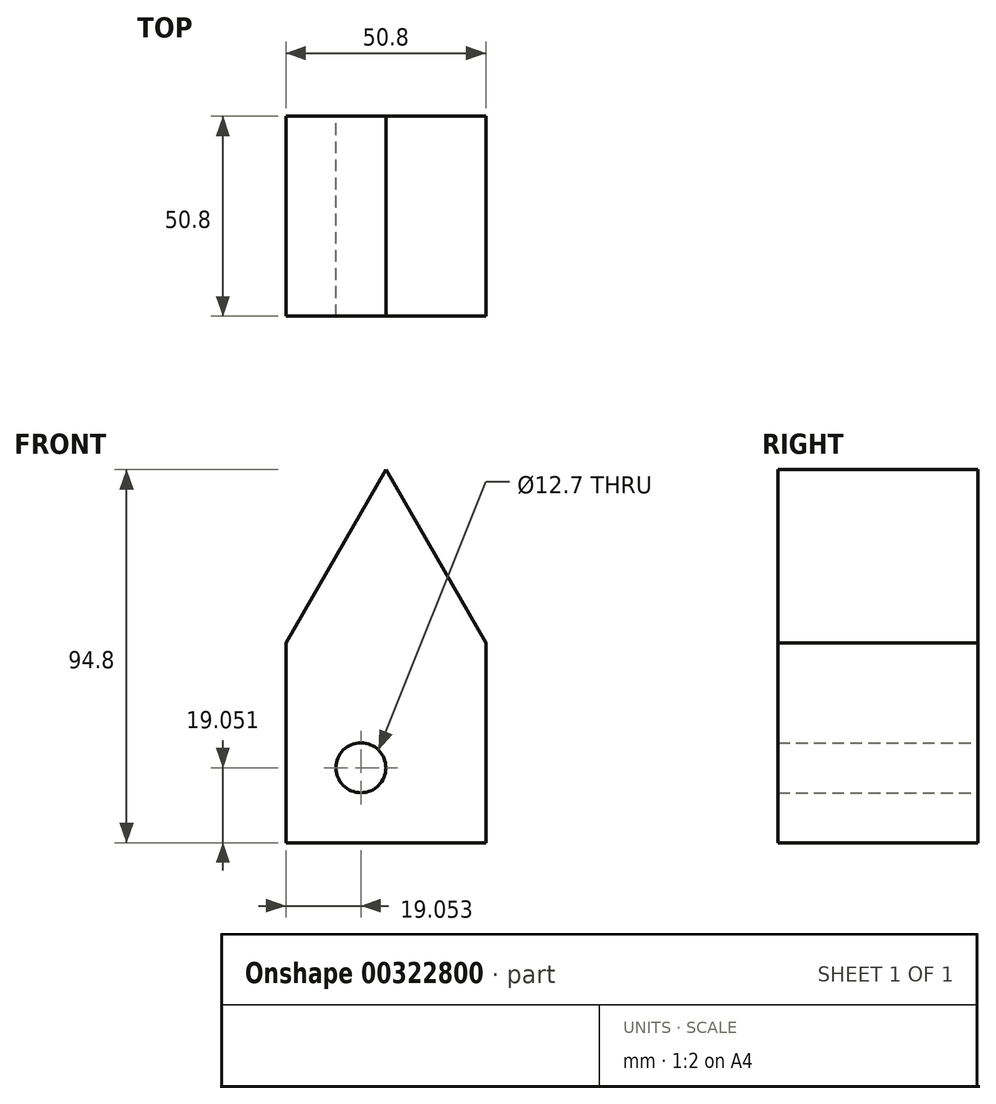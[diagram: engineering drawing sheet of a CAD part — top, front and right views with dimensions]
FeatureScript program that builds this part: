
annotation { "Feature Type Name" : "Feature", "Feature Type Description" : "" }
export const myFeature = defineFeature(function(context is Context, id is Id, definition is map)
    precondition{}
    {
        {
            var Q0;
            Q0=qCreatedBy(makeId("Front.planeOp"),FACE);
            var sketch = newSketch(context, id + "F0", { "sketchPlane" : qUnion([Q0])});
            skLineSegment(sketch, "E0.top", {"start": v(-25.17, -26.3) * mm, "end": v(25.63, -26.3) * mm});
            skLineSegment(sketch, "E0.left", {"start": v(-25.17, 24.5) * mm, "end": v(-25.17, -26.3) * mm});
            skLineSegment(sketch, "E0.right", {"start": v(25.63, 24.5) * mm, "end": v(25.63, -26.3) * mm});
            skLineSegment(sketch, "E1", {"start": v(-25.17, 24.5) * mm, "end": v(0.23, 68.49) * mm});
            skPoint(sketch, "E1.endSnap0", {"position": v(0.23, -26.3) * mm});
            skLineSegment(sketch, "E2", {"start": v(0.23, 68.49) * mm, "end": v(25.63, 24.5) * mm});
            skCircle(sketch, "E3", {"center": v(-6.12, -7.26) * mm, "radius": 6.35 * mm});
            skSolve(sketch);
        }
        {
            var Q0;
            Q0=makeQuery(id+"F0.imprint","IMPRINT",FACE,{"disambiguationData":[TD([[makeQuery(id+"F0.imprint","IMPRINT",EDGE,{"derivedFrom":sQuery(id+"F0.wireOp",EDGE,"E0.top")}),1.0]])]});
            extrude(context, id + "F1", {"entities" : qUnion([Q0]), "depth" : 50.8 * mm});
        }
    });
